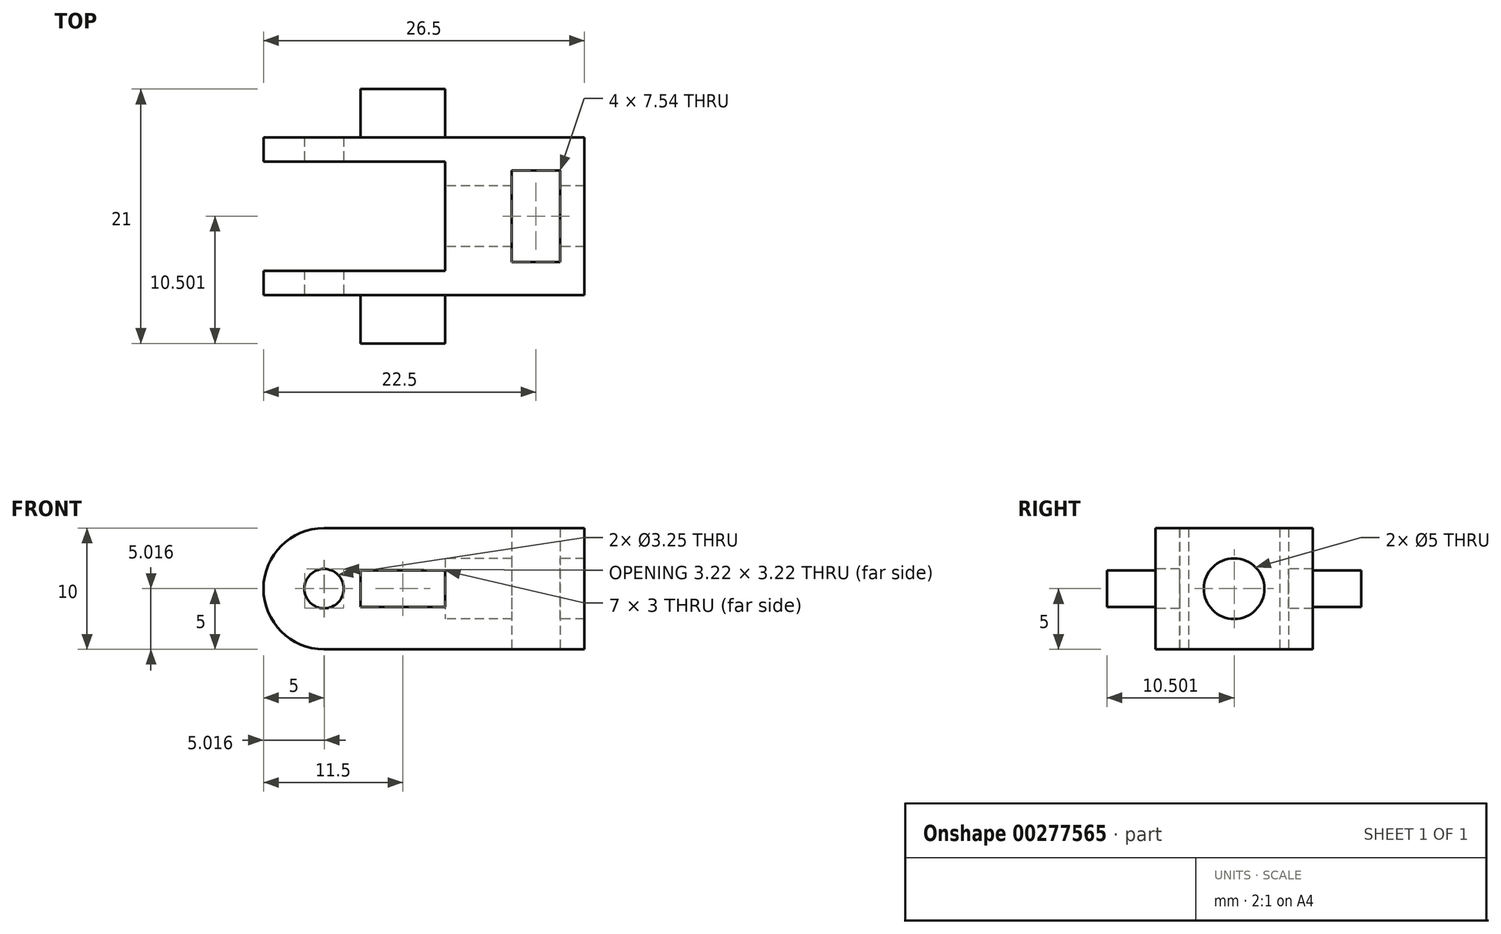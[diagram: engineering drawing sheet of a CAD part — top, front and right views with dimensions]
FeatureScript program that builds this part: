
annotation { "Feature Type Name" : "Feature", "Feature Type Description" : "" }
export const myFeature = defineFeature(function(context is Context, id is Id, definition is map)
    precondition{}
    {
        {
            var Q0;
            Q0=qCreatedBy(makeId("Top.planeOp"),FACE);
            var sketch = newSketch(context, id + "F0", { "sketchPlane" : qUnion([Q0])});
            skLineSegment(sketch, "E0", {"start": v(-15, -6.52) * mm, "end": v(0, -6.52) * mm});
            skLineSegment(sketch, "E1", {"start": v(0, -6.52) * mm, "end": v(0, 0) * mm});
            skLineSegment(sketch, "E2", {"start": v(0, 0) * mm, "end": v(0, 2.48) * mm});
            skLineSegment(sketch, "E3", {"start": v(0, 2.48) * mm, "end": v(-15, 2.48) * mm});
            skLineSegment(sketch, "E4", {"start": v(-15, 2.48) * mm, "end": v(-15, 4.48) * mm});
            skLineSegment(sketch, "E5", {"start": v(-15, 4.48) * mm, "end": v(3, 4.48) * mm});
            skLineSegment(sketch, "E6", {"start": v(3, 4.48) * mm, "end": v(3, -8.52) * mm});
            skLineSegment(sketch, "E7", {"start": v(3, -8.52) * mm, "end": v(-15, -8.52) * mm});
            skLineSegment(sketch, "E8", {"start": v(-15, -8.52) * mm, "end": v(-15, -6.52) * mm});
            skSolve(sketch);
        }
        {
            var Q0;
            Q0=makeQuery(id+"F0.imprint","IMPRINT",FACE,{"disambiguationData":[TD([[makeQuery(id+"F0.imprint","IMPRINT",EDGE,{"derivedFrom":sQuery(id+"F0.wireOp",EDGE,"E0")}),-1.0]])]});
            extrude(context, id + "F1", {"entities" : qUnion([Q0]), "endBound" : BoundingType.SYMMETRIC, "depth" : 10 * mm, "offsetDistance" : 25 * mm});
        }
        {
            var Q0;
            Q0=makeQuery(id+"F1.opExtrude","SWEPT_FACE",FACE,{"disambiguationData":[OSD([sQuery(id+"F0.wireOp",EDGE,"E7")])]});
            var sketch = newSketch(context, id + "F2", { "sketchPlane" : qUnion([Q0])});
            skCircle(sketch, "E9", {"center": v(-10, 0) * mm, "radius": 1.63 * mm});
            skPoint(sketch, "E9.centerSnap0", {"position": v(-15, 0) * mm});
            skCircle(sketch, "E10", {"center": v(-10, 0) * mm, "radius": 5 * mm});
            skSolve(sketch);
        }
        {
            var Q0;
            Q0=makeQuery(id+"F2.imprint","IMPRINT",FACE,{"disambiguationData":[TD([[makeQuery(id+"F2.imprint","IMPRINT",EDGE,{"derivedFrom":sQuery(id+"F2.wireOp",EDGE,"E9")}),1.0]])]});
            extrude(context, id + "F3", {"entities" : qUnion([Q0]), "operationType" : NewBodyOperationType.REMOVE, "oppositeDirection" : true, "depth" : 25 * mm, "offsetDistance" : 25 * mm});
        }
        {
            var Q0;
            {var subQ0=sQuery(id+"F2.wireOp",EDGE,"E10");var subQ1=sQuery(id+"F0.wireOp",EDGE,"E7");var subQ4=makeQuery(id+"F1.opExtrude","CAP_EDGE",EDGE,{"disambiguationData":[OSD([subQ1])],"isStart":false});var subQ5=makeQuery(id+"F2.imprint","INTERSECT",VERTEX,{"derivedFrom":[subQ4,subQ0]});Q0=makeQuery(id+"F2.imprint","IMPRINT",FACE,{"disambiguationData":[TD([[makeQuery(id+"F2.imprint","IMPRINT",EDGE,{"disambiguationData":[TD([[subQ5,-1.0]])],"derivedFrom":subQ0}),-1.0]])]});}
            var Q1;
            {var subQ0=sQuery(id+"F2.wireOp",EDGE,"E10");var subQ1=sQuery(id+"F0.wireOp",EDGE,"E7");var subQ4=makeQuery(id+"F1.opExtrude","CAP_EDGE",EDGE,{"disambiguationData":[OSD([subQ1])],"isStart":true});var subQ5=makeQuery(id+"F2.imprint","INTERSECT",VERTEX,{"derivedFrom":[subQ4,subQ0]});Q1=makeQuery(id+"F2.imprint","IMPRINT",FACE,{"disambiguationData":[TD([[makeQuery(id+"F2.imprint","IMPRINT",EDGE,{"disambiguationData":[TD([[subQ5,1.0]])],"derivedFrom":subQ0}),-1.0]])]});}
            extrude(context, id + "F4", {"entities" : qUnion([Q0, Q1]), "operationType" : NewBodyOperationType.REMOVE, "oppositeDirection" : true, "depth" : 25 * mm, "offsetDistance" : 25 * mm});
        }
        {
            var Q0;
            Q0=makeQuery(id+"F1.opExtrude","SWEPT_FACE",FACE,{"disambiguationData":[OSD([sQuery(id+"F0.wireOp",EDGE,"E7")])]});
            var sketch = newSketch(context, id + "F5", { "sketchPlane" : qUnion([Q0])});
            skLineSegment(sketch, "E11", {"start": v(0, 0) * mm, "end": v(-3.5, 0) * mm});
            skLineSegment(sketch, "E12.bottom", {"start": v(0, 1.5) * mm, "end": v(-7, 1.5) * mm});
            skLineSegment(sketch, "E12.top", {"start": v(0, -1.5) * mm, "end": v(-7, -1.5) * mm});
            skLineSegment(sketch, "E12.left", {"start": v(0, 1.5) * mm, "end": v(0, -1.5) * mm});
            skLineSegment(sketch, "E12.right", {"start": v(-7, 1.5) * mm, "end": v(-7, -1.5) * mm});
            skPoint(sketch, "E12.middle", {"position": v(-3.5, 0) * mm});
            skSolve(sketch);
        }
        {
            var Q0;
            {var subQ3=sQuery(id+"F5.wireOp",EDGE,"E12.bottom");Q0=makeQuery(id+"F5.imprint","IMPRINT",FACE,{"disambiguationData":[TD([[makeQuery(id+"F5.imprint","IMPRINT",EDGE,{"derivedFrom":subQ3}),1.0]])]});}
            extrude(context, id + "F6", {"entities" : qUnion([Q0]), "operationType" : NewBodyOperationType.ADD, "depth" : 4 * mm, "offsetDistance" : 25 * mm});
        }
        {
            var Q0;
            Q0=makeQuery(id+"F1.opExtrude","SWEPT_FACE",FACE,{"disambiguationData":[OSD([sQuery(id+"F0.wireOp",EDGE,"E5")])]});
            var sketch = newSketch(context, id + "F7", { "sketchPlane" : qUnion([Q0])});
            skLineSegment(sketch, "E13.bottom", {"start": v(0, 1.5) * mm, "end": v(7, 1.5) * mm});
            skLineSegment(sketch, "E13.top", {"start": v(0, -1.5) * mm, "end": v(7, -1.5) * mm});
            skLineSegment(sketch, "E13.left", {"start": v(0, 1.5) * mm, "end": v(0, -1.5) * mm});
            skLineSegment(sketch, "E13.right", {"start": v(7, 1.5) * mm, "end": v(7, -1.5) * mm});
            skPoint(sketch, "E13.middle", {"position": v(3.5, 0) * mm});
            skSolve(sketch);
        }
        {
            var Q0;
            Q0 = qSketchRegion(id + "F7", true);
            extrude(context, id + "F8", {"entities" : qUnion([Q0]), "operationType" : NewBodyOperationType.ADD, "depth" : 4 * mm, "offsetDistance" : 25 * mm});
        }
        {
            var Q0;
            Q0=makeQuery(id+"F1.opExtrude","SWEPT_FACE",FACE,{"disambiguationData":[OSD([sQuery(id+"F0.wireOp",EDGE,"E6")])]});
            extrude(context, id + "F9", {"entities" : qUnion([Q0]), "operationType" : NewBodyOperationType.ADD, "depth" : 1.5 * mm, "offsetDistance" : 25 * mm});
        }
        {
            var Q0;
            Q0=makeQuery(id+"F1.opExtrude","SWEPT_FACE",FACE,{"disambiguationData":[OSD([sQuery(id+"F0.wireOp",EDGE,"E1"),sQuery(id+"F0.wireOp",EDGE,"E2")])]});
            var sketch = newSketch(context, id + "F10", { "sketchPlane" : qUnion([Q0])});
            skPoint(sketch, "E14", {"position": v(2.02, 0) * mm});
            skPoint(sketch, "E14.positionSnap0", {"position": v(8.52, 0) * mm});
            skPoint(sketch, "E14.positionSnap1", {"position": v(2.02, 5) * mm});
            skSolve(sketch);
        }
        {
            var Q0;
            Q0=makeQuery(id+"F9.opExtrude","CAP_FACE",FACE,{"disambiguationData":[OSD([sQuery(id+"F0.wireOp",EDGE,"E6")])],"isStart":false});
            extrude(context, id + "F11", {"entities" : qUnion([Q0]), "operationType" : NewBodyOperationType.ADD, "depth" : 7 * mm, "offsetDistance" : 25 * mm});
        }
        {
            var Q0;
            {var subQ0=sQuery(id+"F0.wireOp",EDGE,"E6");var subQ1=makeQuery(id+"F1.opExtrude","CAP_EDGE",EDGE,{"disambiguationData":[OSD([subQ0])],"isStart":true});Q0=makeQuery(id+"F11.boolean.opBoolean","MERGE",FACE,{"derivedFrom":[makeQuery(id+"F9.boolean.opBoolean","MERGE",FACE,{"derivedFrom":[makeQuery(id+"F1.opExtrude","CAP_FACE",FACE,{"disambiguationData":[OSD([sQuery(id+"F0.wireOp",EDGE,"E0"),sQuery(id+"F0.wireOp",EDGE,"E1"),sQuery(id+"F0.wireOp",EDGE,"E2"),sQuery(id+"F0.wireOp",EDGE,"E3"),sQuery(id+"F0.wireOp",EDGE,"E4"),sQuery(id+"F0.wireOp",EDGE,"E5"),subQ0,sQuery(id+"F0.wireOp",EDGE,"E7"),sQuery(id+"F0.wireOp",EDGE,"E8")])],"isStart":true}),makeQuery(id+"F9.opExtrude","SWEPT_FACE",FACE,{"disambiguationData":[OSD([subQ0]),TDD([subQ1])]})]}),makeQuery(id+"F11.opExtrude","SWEPT_FACE",FACE,{"disambiguationData":[OSD([subQ0]),TDD([makeQuery(id+"F9.opExtrude","CAP_EDGE",EDGE,{"disambiguationData":[OSD([subQ0]),TDD([subQ1])],"isStart":false})])]})]});}
            var sketch = newSketch(context, id + "F12", { "sketchPlane" : qUnion([Q0])});
            skLineSegment(sketch, "E15", {"start": v(11.5, 2.02) * mm, "end": v(9.5, 2.02) * mm});
            skLineSegment(sketch, "E16", {"start": v(9.5, 2.02) * mm, "end": v(9.5, 5.79) * mm});
            skLineSegment(sketch, "E17", {"start": v(9.5, 5.79) * mm, "end": v(5.5, 5.79) * mm});
            skLineSegment(sketch, "E18", {"start": v(5.5, 5.79) * mm, "end": v(5.5, -1.75) * mm});
            skLineSegment(sketch, "E19", {"start": v(5.5, -1.75) * mm, "end": v(9.5, -1.75) * mm});
            skLineSegment(sketch, "E20", {"start": v(9.5, -1.75) * mm, "end": v(9.5, 2.02) * mm});
            skSolve(sketch);
        }
        {
            var Q0;
            Q0 = qSketchRegion(id + "F12", true);
            extrude(context, id + "F13", {"entities" : qUnion([Q0]), "operationType" : NewBodyOperationType.REMOVE, "oppositeDirection" : true, "depth" : 25 * mm, "offsetDistance" : 25 * mm});
        }
        {
            var Q0;
            Q0=sQuery(id+"F10.wireOp",VERTEX,"E14");
            var Q1;
            Q1=makeQuery(id+"F1.opExtrude","SWEPT_BODY",BODY,{"disambiguationData":[OSD([sQuery(id+"F0.wireOp",EDGE,"E0"),sQuery(id+"F0.wireOp",EDGE,"E1"),sQuery(id+"F0.wireOp",EDGE,"E2"),sQuery(id+"F0.wireOp",EDGE,"E3"),sQuery(id+"F0.wireOp",EDGE,"E4"),sQuery(id+"F0.wireOp",EDGE,"E5"),sQuery(id+"F0.wireOp",EDGE,"E6"),sQuery(id+"F0.wireOp",EDGE,"E7"),sQuery(id+"F0.wireOp",EDGE,"E8")])]});
            hole(context, id + "F14", {"style" : HoleStyle.SIMPLE, "endStyle" : HoleEndStyle.BLIND, "holeDiameter" : 5 * mm, "majorDiameter" : 5 * mm, "holeDepth" : 20 * mm, "tappedDepth" : 12 * mm, "tapClearance" : 3, "locations" : qUnion([Q0]), "scope" : qUnion([Q1])});
        }
    });
